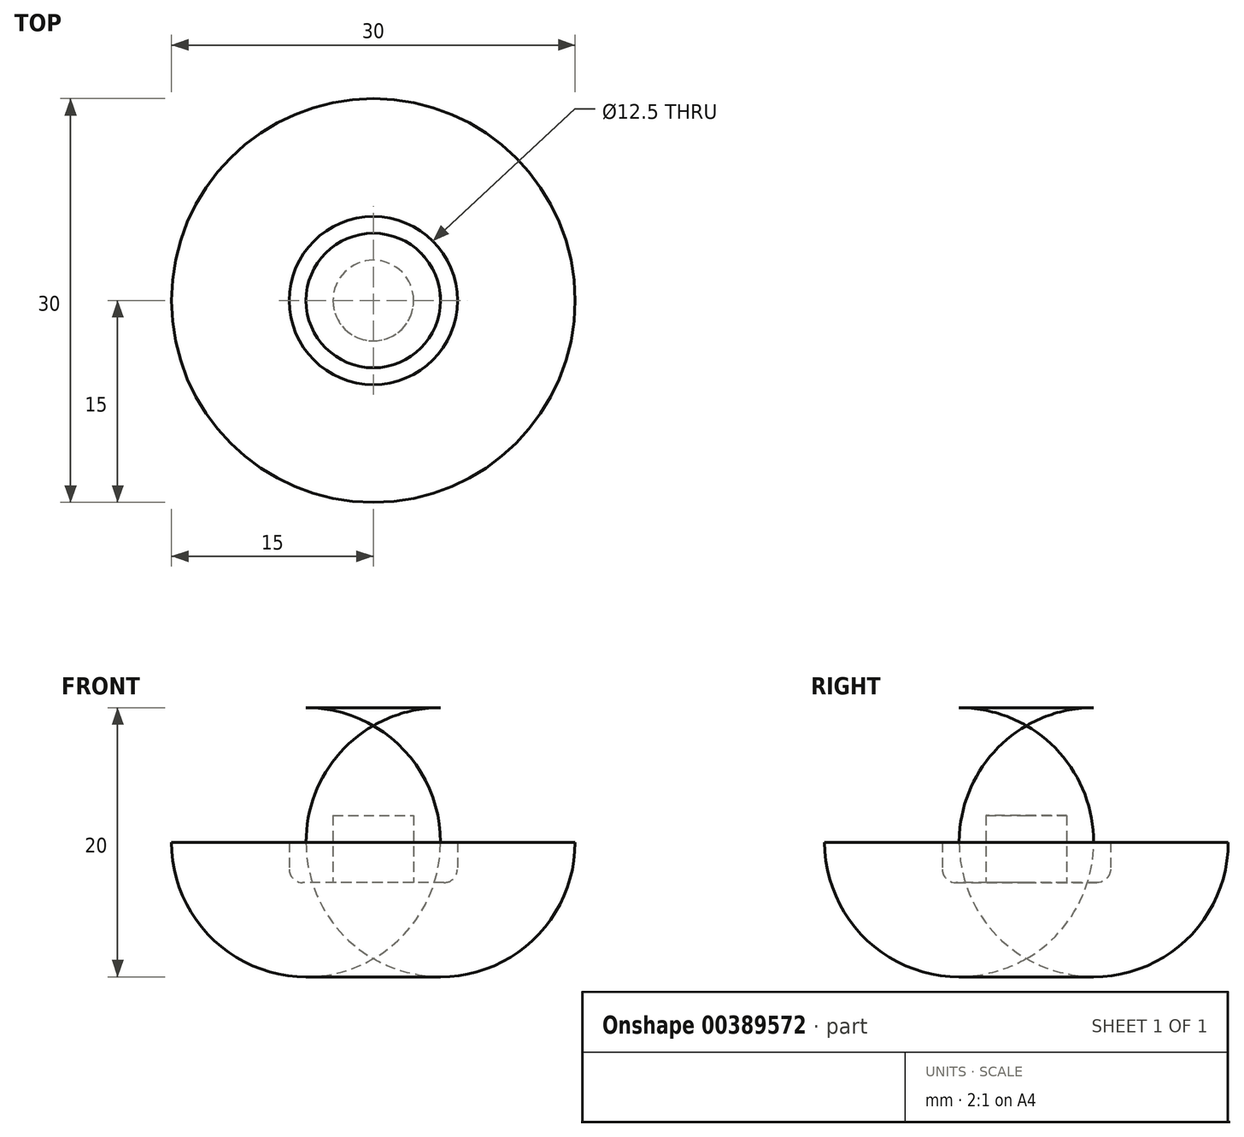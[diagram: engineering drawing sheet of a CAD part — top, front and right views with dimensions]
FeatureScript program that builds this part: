
annotation { "Feature Type Name" : "Feature", "Feature Type Description" : "" }
export const myFeature = defineFeature(function(context is Context, id is Id, definition is map)
    precondition{}
    {
        {
            var Q0;
            Q0=qCreatedBy(makeId("Top.planeOp"),FACE);
            var sketch = newSketch(context, id + "F0", { "sketchPlane" : qUnion([Q0])});
            skCircle(sketch, "E0", {"center": v(0, 0) * mm, "radius": 3 * mm});
            skCircle(sketch, "E1", {"center": v(0, 0) * mm, "radius": 6.25 * mm});
            skSolve(sketch);
        }
        {
            var Q0;
            Q0 = qSketchRegion(id + "F0", true);
            extrude(context, id + "F1", {"entities" : qUnion([Q0]), "depth" : 3 * mm});
        }
        {
            var Q0;
            Q0=qCreatedBy(makeId("Front.planeOp"),FACE);
            var sketch = newSketch(context, id + "F2", { "sketchPlane" : qUnion([Q0])});
            skPoint(sketch, "E2.visualSharp", {"position": v(18.78, 30.05) * mm});
            skLineSegment(sketch, "E3", {"start": v(0, 0) * mm, "end": v(0, 13) * mm, "construction": true});
            skLineSegment(sketch, "E4.bottom", {"start": v(0, 13) * mm, "end": v(5, 13) * mm});
            skLineSegment(sketch, "E4.top", {"start": v(0, 3) * mm, "end": v(15, 3) * mm});
            skLineSegment(sketch, "E4.left", {"start": v(0, 13) * mm, "end": v(0, 3) * mm});
            skLineSegment(sketch, "E4.right", {"start": v(15, 3) * mm, "end": v(15, 3) * mm});
            skPoint(sketch, "E5.visualSharp", {"position": v(15, 13) * mm});
            skArc(sketch, "E5.filletArc", {"start": v(15, 3) * mm, "mid": v(12.07, 10.07) * mm, "end": v(5, 13) * mm});
            skSolve(sketch);
        }
        {
            var Q0;
            Q0 = qSketchRegion(id + "F2", true);
            var Q1;
            Q1=sQuery(id+"F2.wireOp",EDGE,"E3");
            revolve(context, id + "F3", {"operationType" : NewBodyOperationType.ADD, "entities" : qUnion([Q0]), "axis" : qUnion([Q1]), "revolveType" : RevolveType.FULL});
        }
        {
            var Q0;
            Q0=makeQuery(id+"F3.opRevolve","SWEPT_EDGE",EDGE,{"disambiguationData":[OSD([sQuery(id+"F2.wireOp",EDGE,"BL2G8uJJ-2Xtw-oN9y-Opnc-I2waAUdsLUTv"),sQuery(id+"F2.wireOp",EDGE,"E2.filletArc")])]});
            var Q1;
            Q1=makeQuery(id+"F1.opExtrude","CAP_EDGE",EDGE,{"disambiguationData":[OSD([sQuery(id+"F0.wireOp",EDGE,"E1")])],"isStart":true});
            var Q2;
            Q2=makeQuery(id+"F1.opExtrude","CAP_EDGE",EDGE,{"disambiguationData":[OSD([sQuery(id+"F0.wireOp",EDGE,"E1")])],"isStart":false});
            fillet(context, id + "F4", {"entities" : qUnion([Q0, Q1, Q2]), "radius" : 1 * mm, "tangentPropagation" : true, "allowEdgeOverflow" : false});
        }
        {
            var Q0;
            Q0=makeQuery(id+"F3.boolean.opBoolean","SPLIT",FACE,{"disambiguationData":[TD([makeQuery(id+"F1.opExtrude","SWEPT_FACE",FACE,{"disambiguationData":[OSD([sQuery(id+"F0.wireOp",EDGE,"E0")])]})])],"derivedFrom":makeQuery(id+"F3.opRevolve","SWEPT_FACE",FACE,{"disambiguationData":[OSD([sQuery(id+"F2.wireOp",EDGE,"E4.top")])]})});
            extrude(context, id + "F5", {"entities" : qUnion([Q0]), "operationType" : NewBodyOperationType.REMOVE, "oppositeDirection" : true, "depth" : 2 * mm});
        }
    });
